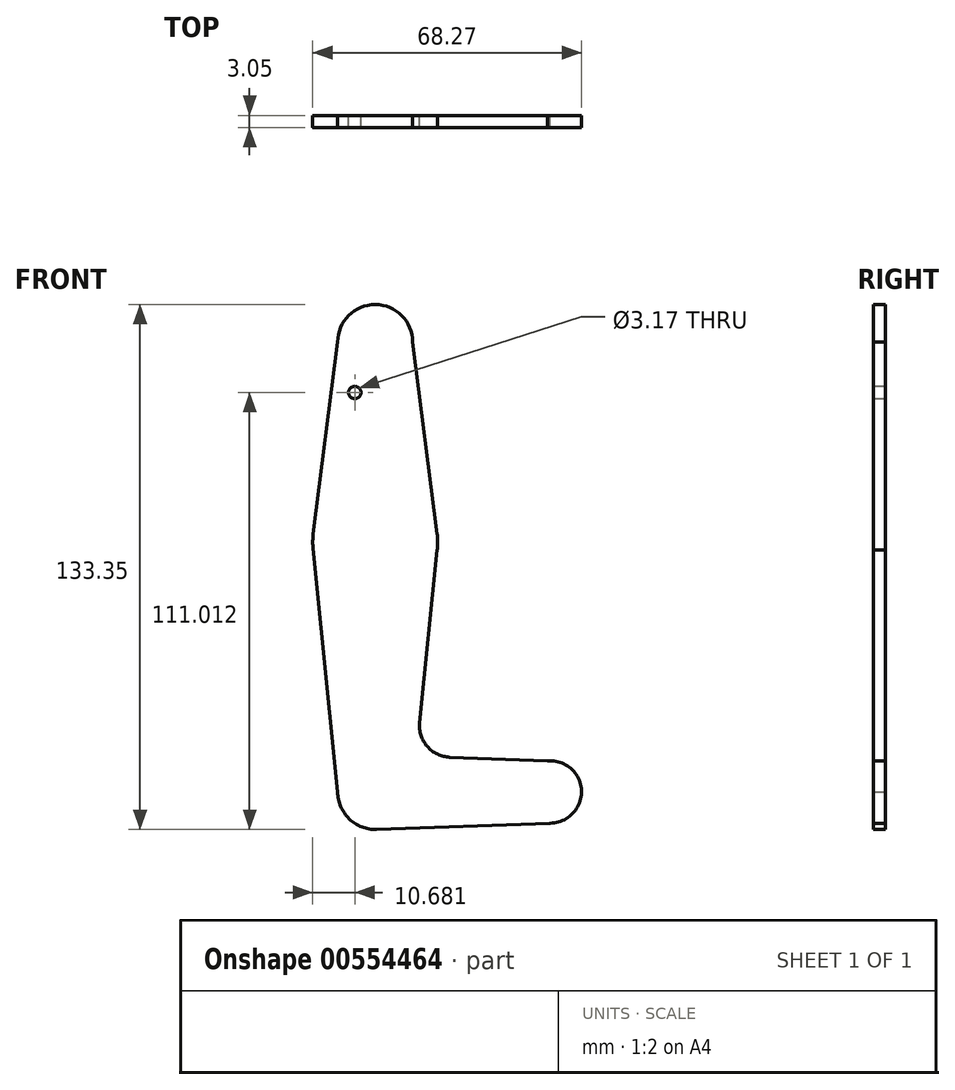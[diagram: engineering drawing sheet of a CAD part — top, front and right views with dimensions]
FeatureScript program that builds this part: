
annotation { "Feature Type Name" : "Feature", "Feature Type Description" : "" }
export const myFeature = defineFeature(function(context is Context, id is Id, definition is map)
    precondition{}
    {
        {
            var Q0;
            Q0=qCreatedBy(makeId("Front.planeOp"),FACE);
            var sketch = newSketch(context, id + "F0", { "sketchPlane" : qUnion([Q0])});
            skCircle(sketch, "E0", {"center": v(0, 0) * mm, "radius": 9.53 * mm});
            skLineSegment(sketch, "E1", {"start": v(0, 0) * mm, "end": v(0, -50.8) * mm});
            skCircle(sketch, "E2", {"center": v(0, -50.8) * mm, "radius": 15.88 * mm});
            skLineSegment(sketch, "E3", {"start": v(0, -50.8) * mm, "end": v(0, -114.3) * mm});
            skCircle(sketch, "E4", {"center": v(0, -114.3) * mm, "radius": 9.53 * mm});
            skLineSegment(sketch, "E5", {"start": v(0, -114.3) * mm, "end": v(44.45, -114.3) * mm});
            skCircle(sketch, "E6", {"center": v(44.45, -114.3) * mm, "radius": 7.94 * mm});
            skLineSegment(sketch, "E7", {"start": v(-9.53, 0) * mm, "end": v(-15.75, -48.8) * mm});
            skLineSegment(sketch, "E8", {"start": v(9.53, 0) * mm, "end": v(15.75, -48.8) * mm});
            skLineSegment(sketch, "E9", {"start": v(15.75, -52.8) * mm, "end": v(11.3, -96.72) * mm});
            skLineSegment(sketch, "E10", {"start": v(-9.53, -114.3) * mm, "end": v(-15.8, -52.4) * mm});
            skLineSegment(sketch, "E11", {"start": v(43.78, -106.4) * mm, "end": v(18.92, -105.47) * mm});
            skLineSegment(sketch, "E12", {"start": v(44.45, -122.24) * mm, "end": v(0, -123.83) * mm});
            skPoint(sketch, "E13.newPointA", {"position": v(0, -104.77) * mm});
            skArc(sketch, "E13.filletArc", {"start": v(11.3, -96.72) * mm, "mid": v(13.22, -102.75) * mm, "end": v(18.92, -105.47) * mm});
            skCircle(sketch, "E14", {"center": v(-5.2, -12.82) * mm, "radius": 1.59 * mm});
            skSolve(sketch);
        }
        {
            var Q0;
            {var subQ0=sQuery(id+"F0.wireOp",EDGE,"E0");var subQ1=makeQuery(id+"F0.imprint","INTERSECT",VERTEX,{"derivedFrom":[subQ0,sQuery(id+"F0.wireOp",EDGE,"E7")]});Q0=makeQuery(id+"F0.imprint","IMPRINT",FACE,{"disambiguationData":[TD([[makeQuery(id+"F0.imprint","IMPRINT",EDGE,{"disambiguationData":[TD([[subQ1,1.0]])],"derivedFrom":subQ0}),1.0]])]});}
            var Q1;
            {var subQ0=sQuery(id+"F0.wireOp",EDGE,"E6");var subQ1=makeQuery(id+"F0.imprint","INTERSECT",VERTEX,{"derivedFrom":[subQ0,sQuery(id+"F0.wireOp",EDGE,"E11")]});Q1=makeQuery(id+"F0.imprint","IMPRINT",FACE,{"disambiguationData":[TD([[makeQuery(id+"F0.imprint","IMPRINT",EDGE,{"disambiguationData":[TD([[subQ1,-1.0]])],"derivedFrom":subQ0}),1.0]])]});}
            var Q2;
            {var subQ0=sQuery(id+"F0.wireOp",EDGE,"E8");Q2=makeQuery(id+"F0.imprint","IMPRINT",FACE,{"disambiguationData":[TD([[makeQuery(id+"F0.imprint","IMPRINT",EDGE,{"derivedFrom":subQ0}),-1.0]])]});}
            var Q3;
            {var subQ3=sQuery(id+"F0.wireOp",EDGE,"E1");var subQ5=sQuery(id+"F0.wireOp",EDGE,"E3");var subQ7=makeQuery(id+"F0.imprint","INTERSECT",VERTEX,{"derivedFrom":[subQ3,subQ5]});Q3=makeQuery(id+"F0.imprint","IMPRINT",FACE,{"disambiguationData":[TD([[makeQuery(id+"F0.imprint","IMPRINT",EDGE,{"disambiguationData":[TD([[subQ7,1.0]])],"derivedFrom":subQ3}),1.0]])]});}
            var Q4;
            {var subQ2=sQuery(id+"F0.wireOp",EDGE,"E3");var subQ5=sQuery(id+"F0.wireOp",EDGE,"E1");var subQ7=makeQuery(id+"F0.imprint","INTERSECT",VERTEX,{"derivedFrom":[subQ5,subQ2]});Q4=makeQuery(id+"F0.imprint","IMPRINT",FACE,{"disambiguationData":[TD([[makeQuery(id+"F0.imprint","IMPRINT",EDGE,{"disambiguationData":[TD([[subQ7,1.0]])],"derivedFrom":subQ5}),-1.0]])]});}
            var Q5;
            {var subQ0=sQuery(id+"F0.wireOp",EDGE,"E12");var subQ1=sQuery(id+"F0.wireOp",EDGE,"E4");var subQ2=makeQuery(id+"F0.imprint","INTERSECT",VERTEX,{"derivedFrom":[subQ1,subQ0]});Q5=makeQuery(id+"F0.imprint","IMPRINT",FACE,{"disambiguationData":[TD([[makeQuery(id+"F0.imprint","IMPRINT",EDGE,{"disambiguationData":[TD([[subQ2,-1.0]])],"derivedFrom":subQ1}),-1.0]])]});}
            var Q6;
            {var subQ0=sQuery(id+"F0.wireOp",EDGE,"E7");Q6=makeQuery(id+"F0.imprint","IMPRINT",FACE,{"disambiguationData":[TD([[makeQuery(id+"F0.imprint","IMPRINT",EDGE,{"derivedFrom":subQ0}),1.0]])]});}
            var Q7;
            {var subQ9=sQuery(id+"F0.wireOp",EDGE,"E9");Q7=makeQuery(id+"F0.imprint","IMPRINT",FACE,{"disambiguationData":[TD([[makeQuery(id+"F0.imprint","IMPRINT",EDGE,{"derivedFrom":subQ9}),-1.0]])]});}
            var Q8;
            {var subQ2=sQuery(id+"F0.wireOp",EDGE,"E5");var subQ5=sQuery(id+"F0.wireOp",EDGE,"E3");var subQ7=makeQuery(id+"F0.imprint","INTERSECT",VERTEX,{"derivedFrom":[subQ5,subQ2]});Q8=makeQuery(id+"F0.imprint","IMPRINT",FACE,{"disambiguationData":[TD([[makeQuery(id+"F0.imprint","IMPRINT",EDGE,{"disambiguationData":[TD([[subQ7,1.0]])],"derivedFrom":subQ5}),-1.0]])]});}
            var Q9;
            {var subQ0=sQuery(id+"F0.wireOp",EDGE,"E5");var subQ1=sQuery(id+"F0.wireOp",EDGE,"E3");var subQ2=makeQuery(id+"F0.imprint","INTERSECT",VERTEX,{"derivedFrom":[subQ1,subQ0]});Q9=makeQuery(id+"F0.imprint","IMPRINT",FACE,{"disambiguationData":[TD([[makeQuery(id+"F0.imprint","IMPRINT",EDGE,{"disambiguationData":[TD([[subQ2,1.0]])],"derivedFrom":subQ1}),1.0]])]});}
            var Q10;
            {var subQ0=sQuery(id+"F0.wireOp",EDGE,"E10");Q10=makeQuery(id+"F0.imprint","IMPRINT",FACE,{"disambiguationData":[TD([[makeQuery(id+"F0.imprint","IMPRINT",EDGE,{"derivedFrom":subQ0}),-1.0]])]});}
            extrude(context, id + "F1", {"entities" : qUnion([Q0, Q1, Q2, Q3, Q4, Q5, Q6, Q7, Q8, Q9, Q10]), "depth" : 3.05 * mm, "offsetDistance" : 25.4 * mm});
        }
    });
